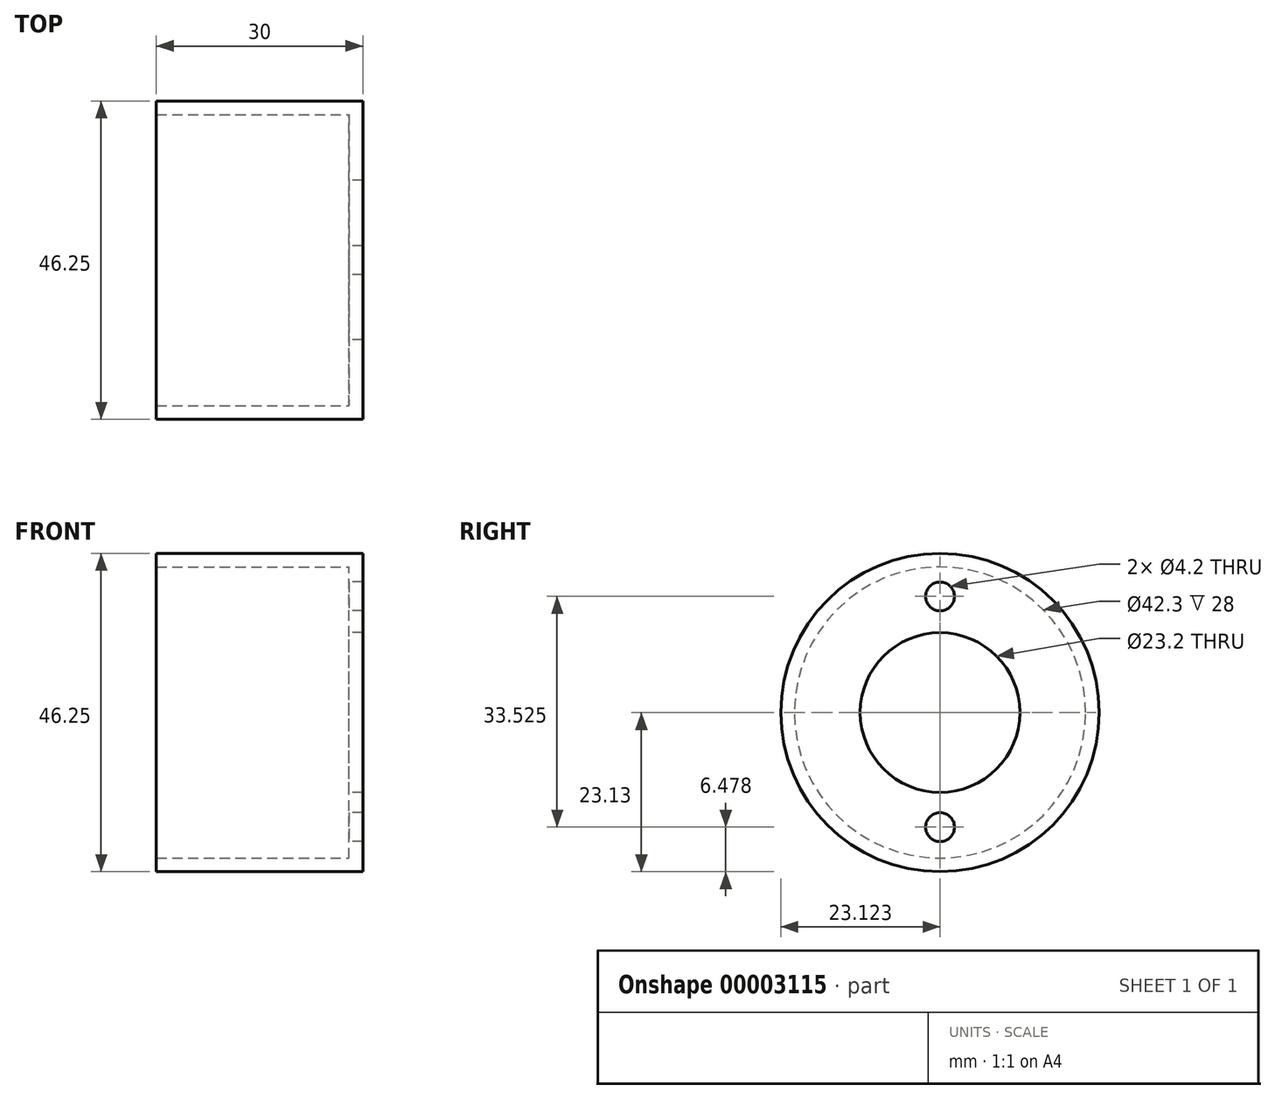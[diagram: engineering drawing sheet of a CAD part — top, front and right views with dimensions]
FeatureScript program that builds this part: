
annotation { "Feature Type Name" : "Feature", "Feature Type Description" : "" }
export const myFeature = defineFeature(function(context is Context, id is Id, definition is map)
    precondition{}
    {
        {
            var Q0;
            Q0=qCreatedBy(makeId("Right.planeOp"),FACE);
            var sketch = newSketch(context, id + "F0", { "sketchPlane" : qUnion([Q0])});
            skCircle(sketch, "E0", {"center": v(0.02, -0.11) * mm, "radius": 23.12 * mm});
            skCircle(sketch, "E1", {"center": v(0.02, -0.11) * mm, "radius": 21.15 * mm});
            skCircle(sketch, "E2", {"center": v(0.02, -0.11) * mm, "radius": 11.6 * mm});
            skCircle(sketch, "E3", {"center": v(0, 0) * mm, "radius": 16.76 * mm, "construction": true});
            skPoint(sketch, "E4", {"position": v(0.02, 16.76) * mm});
            skPoint(sketch, "E5", {"position": v(0.02, -16.76) * mm});
            skSolve(sketch);
        }
        {
            var Q0;
            Q0=makeQuery(id+"F0.imprint","IMPRINT",FACE,{"disambiguationData":[TD([[makeQuery(id+"F0.imprint","IMPRINT",EDGE,{"derivedFrom":sQuery(id+"F0.wireOp",EDGE,"E0")}),1.0]])]});
            extrude(context, id + "F1", {"entities" : qUnion([Q0]), "oppositeDirection" : true, "depth" : 28 * mm});
        }
        {
            var Q0;
            Q0=makeQuery(id+"F0.imprint","IMPRINT",FACE,{"disambiguationData":[TD([[makeQuery(id+"F0.imprint","IMPRINT",EDGE,{"derivedFrom":sQuery(id+"F0.wireOp",EDGE,"E1")}),1.0]])]});
            var Q1;
            Q1=makeQuery(id+"F0.imprint","IMPRINT",FACE,{"disambiguationData":[TD([[makeQuery(id+"F0.imprint","IMPRINT",EDGE,{"derivedFrom":sQuery(id+"F0.wireOp",EDGE,"E0")}),1.0]])]});
            extrude(context, id + "F2", {"entities" : qUnion([Q0, Q1]), "operationType" : NewBodyOperationType.ADD, "depth" : 2 * mm});
        }
        {
            var Q0;
            Q0=sQuery(id+"F0.wireOp",VERTEX,"E4");
            var Q1;
            Q1=sQuery(id+"F0.wireOp",VERTEX,"E5");
            var Q2;
            Q2=makeQuery(id+"F1.opExtrude","SWEPT_BODY",BODY,{"disambiguationData":[OSD([sQuery(id+"F0.wireOp",EDGE,"E0"),sQuery(id+"F0.wireOp",EDGE,"E1")])]});
            hole(context, id + "F3", {"style" : HoleStyle.SIMPLE, "endStyle" : HoleEndStyle.THROUGH, "oppositeDirection" : true, "standardTappedOrClearance" : lookupTablePath({ "standard" : "ISO", "engagement" : "75%", "pitch" : "0.8 mm", "size" : "M5", "type" : "Tapped" }), "standardBlindInLast" : lookupTablePath({ "standard" : "ISO", "engagement" : "75%", "pitch" : "0.8 mm", "size" : "M5", "type" : "Tapped" }), "holeDiameter" : 4.2 * mm, "showTappedDepth" : true, "tappedDepth" : 14.25 * mm, "tapClearance" : 3, "startFromSketch" : true, "locations" : qUnion([Q0, Q1]), "scope" : qUnion([Q2]), "majorDiameter" : 5 * mm});
        }
    });
